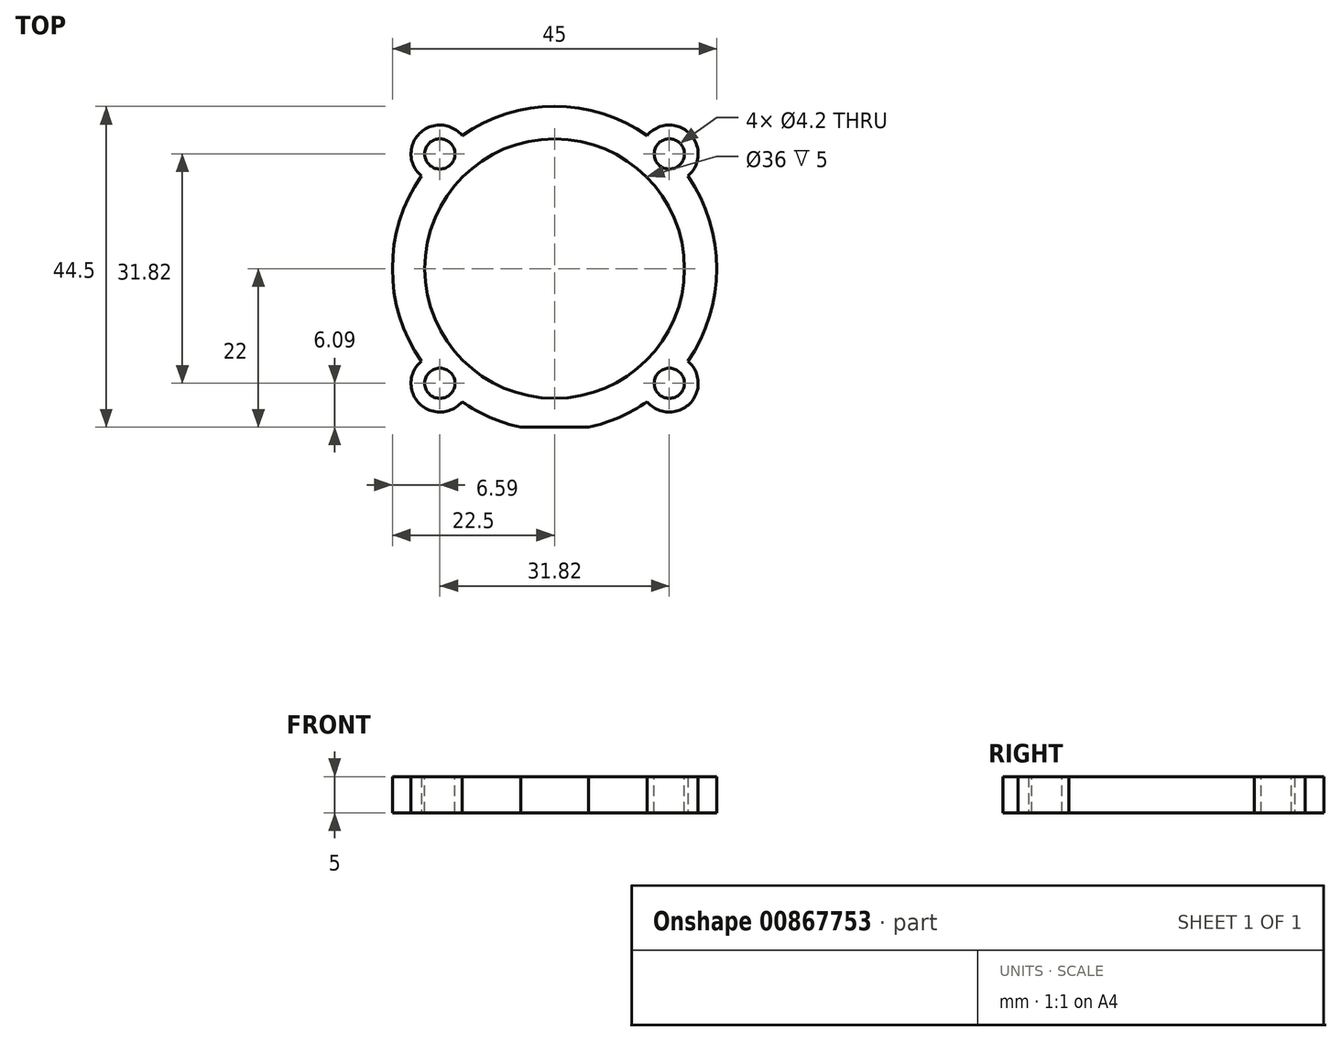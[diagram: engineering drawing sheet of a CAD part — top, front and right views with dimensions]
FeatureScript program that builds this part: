
annotation { "Feature Type Name" : "Feature", "Feature Type Description" : "" }
export const myFeature = defineFeature(function(context is Context, id is Id, definition is map)
    precondition{}
    {
        {
            var Q0;
            Q0=qCreatedBy(makeId("Top.planeOp"),FACE);
            var sketch = newSketch(context, id + "F0", { "sketchPlane" : qUnion([Q0])});
            skArc(sketch, "E0", {"start": v(12.84, 18.48) * mm, "mid": v(0, 22.5) * mm, "end": v(-12.84, 18.48) * mm});
            skLineSegment(sketch, "E1", {"start": v(0, 0) * mm, "end": v(-27.58, 27.58) * mm, "construction": true});
            skLineSegment(sketch, "E2", {"start": v(0, 0) * mm, "end": v(35.21, 35.21) * mm, "construction": true});
            skLineSegment(sketch, "E3", {"start": v(0, 0) * mm, "end": v(26.29, -26.29) * mm, "construction": true});
            skLineSegment(sketch, "E4", {"start": v(0, 0) * mm, "end": v(-25.6, -25.6) * mm, "construction": true});
            skArc(sketch, "E5", {"start": v(-12.84, 18.48) * mm, "mid": v(-18.74, 18.74) * mm, "end": v(-18.48, 12.84) * mm});
            skArc(sketch, "E6", {"start": v(18.48, 12.84) * mm, "mid": v(18.74, 18.74) * mm, "end": v(12.84, 18.48) * mm});
            skArc(sketch, "E7", {"start": v(12.84, -18.48) * mm, "mid": v(18.74, -18.74) * mm, "end": v(18.48, -12.84) * mm});
            skArc(sketch, "E8", {"start": v(-18.48, -12.84) * mm, "mid": v(-18.74, -18.74) * mm, "end": v(-12.84, -18.48) * mm});
            skArc(sketch, "E9.trimOffspring", {"start": v(-18.48, 12.84) * mm, "mid": v(-22.5, 0) * mm, "end": v(-18.48, -12.84) * mm});
            skArc(sketch, "E10.trimOffspring", {"start": v(-12.84, -18.48) * mm, "mid": v(-8.95, -20.64) * mm, "end": v(-4.72, -22) * mm});
            skArc(sketch, "E11.trimOffspring", {"start": v(18.48, -12.84) * mm, "mid": v(22.5, 0) * mm, "end": v(18.48, 12.84) * mm});
            skCircle(sketch, "E12", {"center": v(0, 0) * mm, "radius": 18.63 * mm, "construction": true});
            skLineSegment(sketch, "E13", {"start": v(-4.72, -22) * mm, "end": v(4.72, -22) * mm});
            skArc(sketch, "E14.trimOffspring", {"start": v(4.72, -22) * mm, "mid": v(8.95, -20.64) * mm, "end": v(12.84, -18.48) * mm});
            skSolve(sketch);
        }
        {
            var Q0;
            Q0=qSketchRegion(id+"F0",true);
            extrude(context, id + "F1", {"entities" : qUnion([Q0]), "depth" : 5 * mm, "offsetDistance" : 25 * mm});
        }
        {
            var Q0;
            Q0=makeQuery(id+"F1.opExtrude","CAP_FACE",FACE,{"disambiguationData":[OSD([sQuery(id+"F0.wireOp",EDGE,"E0"),sQuery(id+"F0.wireOp",EDGE,"E5"),sQuery(id+"F0.wireOp",EDGE,"E6"),sQuery(id+"F0.wireOp",EDGE,"E7"),sQuery(id+"F0.wireOp",EDGE,"E8"),sQuery(id+"F0.wireOp",EDGE,"E9.trimOffspring"),sQuery(id+"F0.wireOp",EDGE,"E10.trimOffspring"),sQuery(id+"F0.wireOp",EDGE,"E11.trimOffspring"),sQuery(id+"F0.wireOp",EDGE,"E13"),sQuery(id+"F0.wireOp",EDGE,"E14.trimOffspring")])],"isStart":false});
            var sketch = newSketch(context, id + "F2", { "sketchPlane" : qUnion([Q0])});
            skCircle(sketch, "E15", {"center": v(-15.9, 15.9) * mm, "radius": 2.1 * mm});
            skCircle(sketch, "E16", {"center": v(15.9, 15.9) * mm, "radius": 2.1 * mm});
            skCircle(sketch, "E17", {"center": v(15.9, -15.9) * mm, "radius": 2.1 * mm});
            skCircle(sketch, "E18", {"center": v(-15.9, -15.9) * mm, "radius": 2.1 * mm});
            skSolve(sketch);
        }
        {
            var Q0;
            Q0=qSketchRegion(id+"F2",true);
            extrude(context, id + "F3", {"entities" : qUnion([Q0]), "operationType" : NewBodyOperationType.REMOVE, "endBound" : BoundingType.THROUGH_ALL, "oppositeDirection" : true, "depth" : 25 * mm, "offsetDistance" : 25 * mm});
        }
        {
            var Q0;
            Q0=makeQuery(id+"F1.opExtrude","CAP_FACE",FACE,{"disambiguationData":[OSD([sQuery(id+"F0.wireOp",EDGE,"E0"),sQuery(id+"F0.wireOp",EDGE,"E5"),sQuery(id+"F0.wireOp",EDGE,"E6"),sQuery(id+"F0.wireOp",EDGE,"E7"),sQuery(id+"F0.wireOp",EDGE,"E8"),sQuery(id+"F0.wireOp",EDGE,"E9.trimOffspring"),sQuery(id+"F0.wireOp",EDGE,"E10.trimOffspring"),sQuery(id+"F0.wireOp",EDGE,"E11.trimOffspring"),sQuery(id+"F0.wireOp",EDGE,"E13"),sQuery(id+"F0.wireOp",EDGE,"E14.trimOffspring")])],"isStart":false});
            var sketch = newSketch(context, id + "F4", { "sketchPlane" : qUnion([Q0])});
            skCircle(sketch, "E19", {"center": v(0, 0) * mm, "radius": 18 * mm});
            skSolve(sketch);
        }
        {
            var Q0;
            Q0 = qSketchRegion(id + "F4", true);
            extrude(context, id + "F5", {"entities" : qUnion([Q0]), "operationType" : NewBodyOperationType.REMOVE, "endBound" : BoundingType.THROUGH_ALL, "oppositeDirection" : true, "depth" : 25 * mm, "offsetDistance" : 25 * mm});
        }
    });
